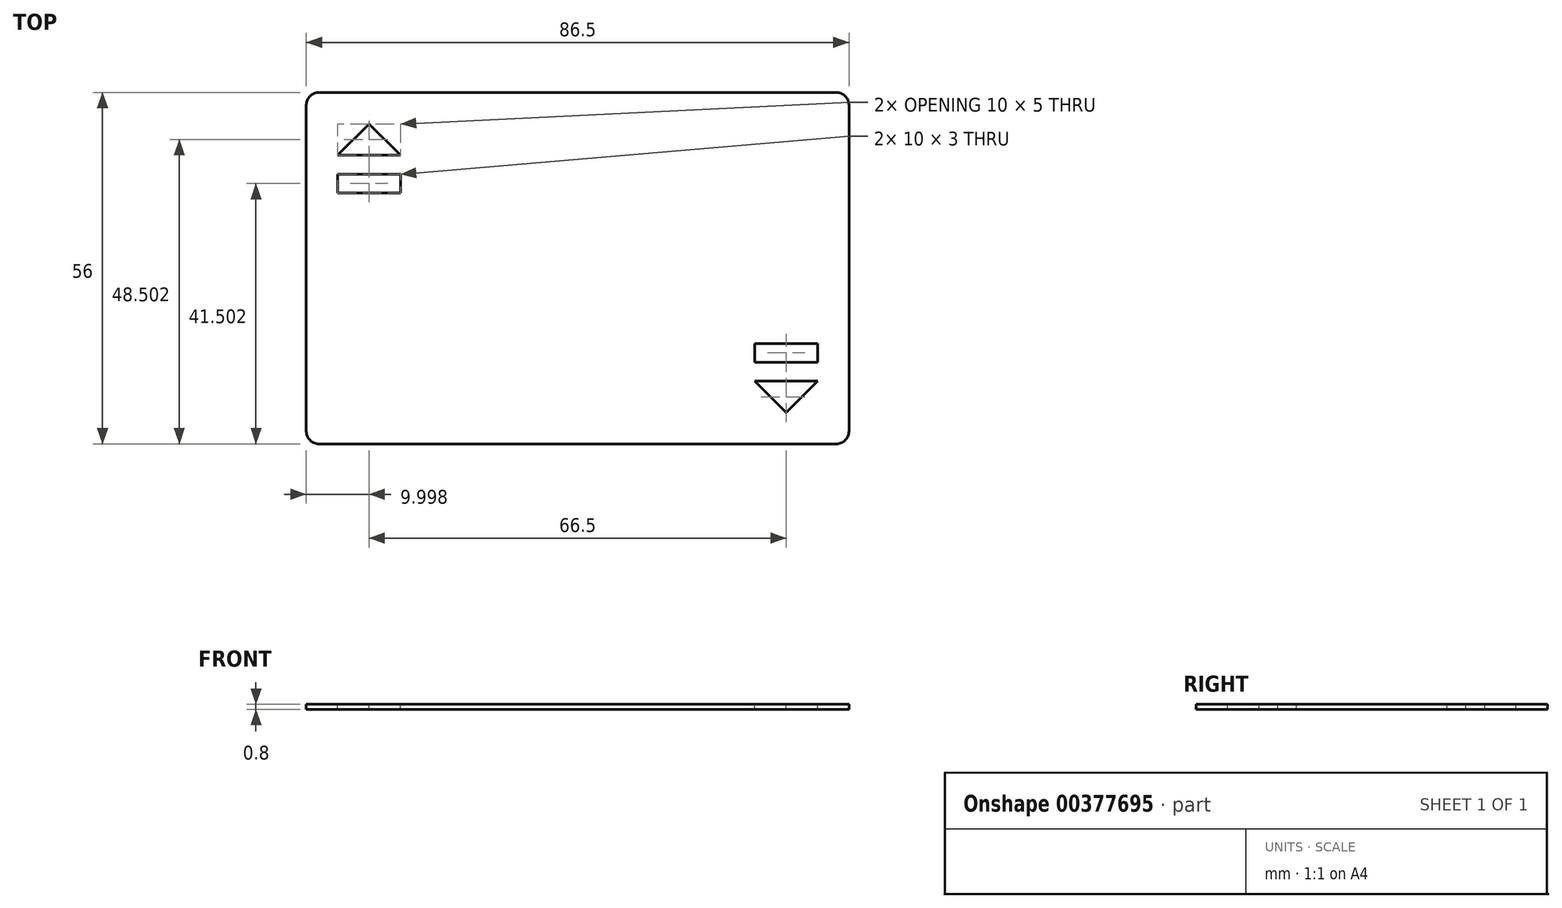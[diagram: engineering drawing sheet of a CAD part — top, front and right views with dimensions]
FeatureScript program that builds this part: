
annotation { "Feature Type Name" : "Feature", "Feature Type Description" : "" }
export const myFeature = defineFeature(function(context is Context, id is Id, definition is map)
    precondition{}
    {
        {
            var Q0;
            Q0=qCreatedBy(makeId("Top.planeOp"),FACE);
            var sketch = newSketch(context, id + "F0", { "sketchPlane" : qUnion([Q0])});
            skLineSegment(sketch, "E0.bottom", {"start": v(-43.73, 24.11) * mm, "end": v(38.77, 24.11) * mm});
            skLineSegment(sketch, "E0.top", {"start": v(-43.73, -31.89) * mm, "end": v(38.77, -31.89) * mm});
            skLineSegment(sketch, "E0.left", {"start": v(-45.73, 22.11) * mm, "end": v(-45.73, -29.89) * mm});
            skLineSegment(sketch, "E0.right", {"start": v(40.77, 22.11) * mm, "end": v(40.77, -29.89) * mm});
            skPoint(sketch, "E1.visualSharp", {"position": v(40.77, 24.11) * mm});
            skArc(sketch, "E1.filletArc", {"start": v(40.77, 22.11) * mm, "mid": v(40.18, 23.53) * mm, "end": v(38.77, 24.11) * mm});
            skPoint(sketch, "E2.visualSharp", {"position": v(40.77, -31.89) * mm});
            skArc(sketch, "E2.filletArc", {"start": v(38.77, -31.89) * mm, "mid": v(40.18, -31.3) * mm, "end": v(40.77, -29.89) * mm});
            skPoint(sketch, "E3.visualSharp", {"position": v(-45.73, -31.89) * mm});
            skArc(sketch, "E3.filletArc", {"start": v(-45.73, -29.89) * mm, "mid": v(-45.15, -31.3) * mm, "end": v(-43.73, -31.89) * mm});
            skPoint(sketch, "E4.visualSharp", {"position": v(-45.73, 24.11) * mm});
            skArc(sketch, "E4.filletArc", {"start": v(-43.73, 24.11) * mm, "mid": v(-45.15, 23.53) * mm, "end": v(-45.73, 22.11) * mm});
            skSolve(sketch);
        }
        {
            var Q0;
            Q0 = qSketchRegion(id + "F0", true);
            extrude(context, id + "F1", {"entities" : qUnion([Q0]), "depth" : 0.8 * mm});
        }
        {
            var Q0;
            Q0=makeQuery(id+"F1.opExtrude","CAP_FACE",FACE,{"disambiguationData":[OSD([sQuery(id+"F0.wireOp",EDGE,"E0.bottom"),sQuery(id+"F0.wireOp",EDGE,"E0.top"),sQuery(id+"F0.wireOp",EDGE,"E0.left"),sQuery(id+"F0.wireOp",EDGE,"E0.right"),sQuery(id+"F0.wireOp",EDGE,"E1.filletArc"),sQuery(id+"F0.wireOp",EDGE,"E2.filletArc"),sQuery(id+"F0.wireOp",EDGE,"E3.filletArc"),sQuery(id+"F0.wireOp",EDGE,"E4.filletArc")])],"isStart":false});
            var sketch = newSketch(context, id + "F2", { "sketchPlane" : qUnion([Q0])});
            skLineSegment(sketch, "E5.bottom", {"start": v(-40.73, 8.11) * mm, "end": v(-30.73, 8.11) * mm});
            skLineSegment(sketch, "E5.top", {"start": v(-40.73, 11.11) * mm, "end": v(-30.73, 11.11) * mm});
            skLineSegment(sketch, "E5.left", {"start": v(-40.73, 8.11) * mm, "end": v(-40.73, 11.11) * mm});
            skLineSegment(sketch, "E5.right", {"start": v(-30.73, 8.11) * mm, "end": v(-30.73, 11.11) * mm});
            skLineSegment(sketch, "E6", {"start": v(-40.73, 14.11) * mm, "end": v(-30.73, 14.11) * mm});
            skLineSegment(sketch, "E7", {"start": v(-30.73, 14.11) * mm, "end": v(-35.73, 19.11) * mm});
            skLineSegment(sketch, "E8", {"start": v(-35.73, 19.11) * mm, "end": v(-40.73, 14.11) * mm});
            skLineSegment(sketch, "E9.bottom", {"start": v(35.77, -15.89) * mm, "end": v(25.77, -15.89) * mm});
            skLineSegment(sketch, "E9.top", {"start": v(35.77, -18.89) * mm, "end": v(25.77, -18.89) * mm});
            skLineSegment(sketch, "E9.left", {"start": v(35.77, -15.89) * mm, "end": v(35.77, -18.89) * mm});
            skLineSegment(sketch, "E9.right", {"start": v(25.77, -15.89) * mm, "end": v(25.77, -18.89) * mm});
            skLineSegment(sketch, "E10", {"start": v(35.77, -21.89) * mm, "end": v(25.77, -21.89) * mm});
            skLineSegment(sketch, "E11", {"start": v(25.77, -21.89) * mm, "end": v(30.77, -26.89) * mm});
            skLineSegment(sketch, "E12", {"start": v(30.77, -26.89) * mm, "end": v(35.77, -21.89) * mm});
            skSolve(sketch);
        }
        {
            var Q0;
            Q0 = qSketchRegion(id + "F2", true);
            extrude(context, id + "F3", {"entities" : qUnion([Q0]), "operationType" : NewBodyOperationType.REMOVE, "oppositeDirection" : true, "depth" : 25 * mm});
        }
    });
